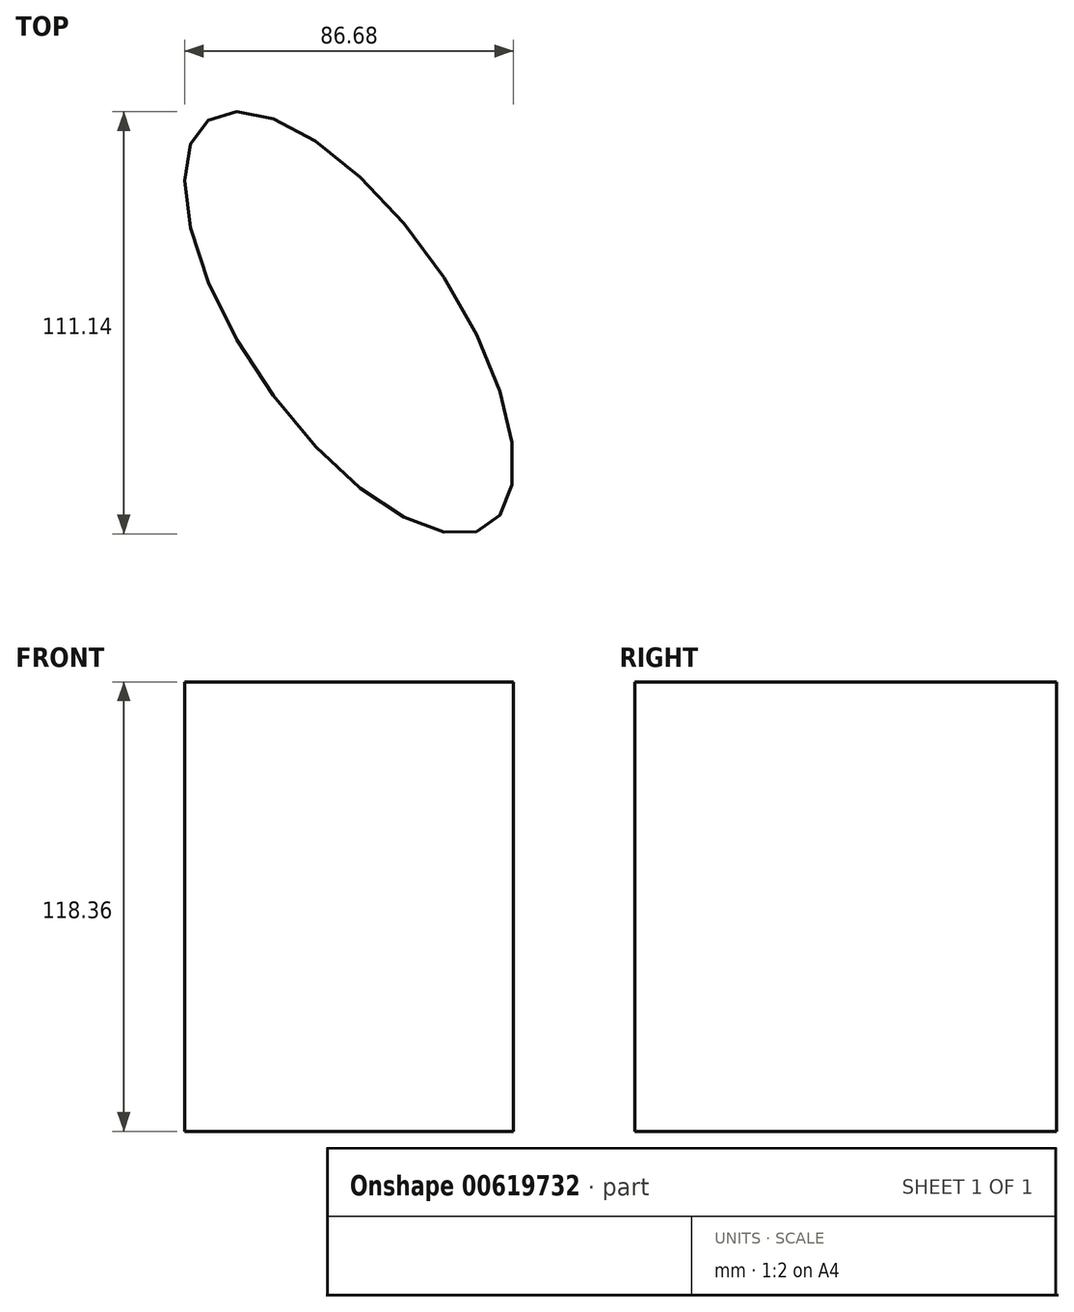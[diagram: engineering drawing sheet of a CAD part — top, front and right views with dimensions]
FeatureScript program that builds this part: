
annotation { "Feature Type Name" : "Feature", "Feature Type Description" : "" }
export const myFeature = defineFeature(function(context is Context, id is Id, definition is map)
    precondition{}
    {
        {
            var Q0;
            Q0=qCreatedBy(makeId("Top.planeOp"),FACE);
            var sketch = newSketch(context, id + "F0", { "sketchPlane" : qUnion([Q0])});
            skEllipse(sketch, "E0", {"center": v(0, 0) * mm, "majorRadius": 64.93 * mm, "minorRadius": 27.4 * mm, "majorAxis": v(-0.57, 0.82)});
            skSolve(sketch);
        }
        {
            var Q0;
            Q0=makeQuery(id+"F0.imprint","IMPRINT",FACE,{"disambiguationData":[TD([[makeQuery(id+"F0.imprint","IMPRINT",EDGE,{"derivedFrom":sQuery(id+"F0.wireOp",EDGE,"E0")}),1.0]])]});
            extrude(context, id + "F1", {"entities" : qUnion([Q0]), "depth" : 118.36 * mm, "offsetDistance" : 25.4 * mm});
        }
    });
